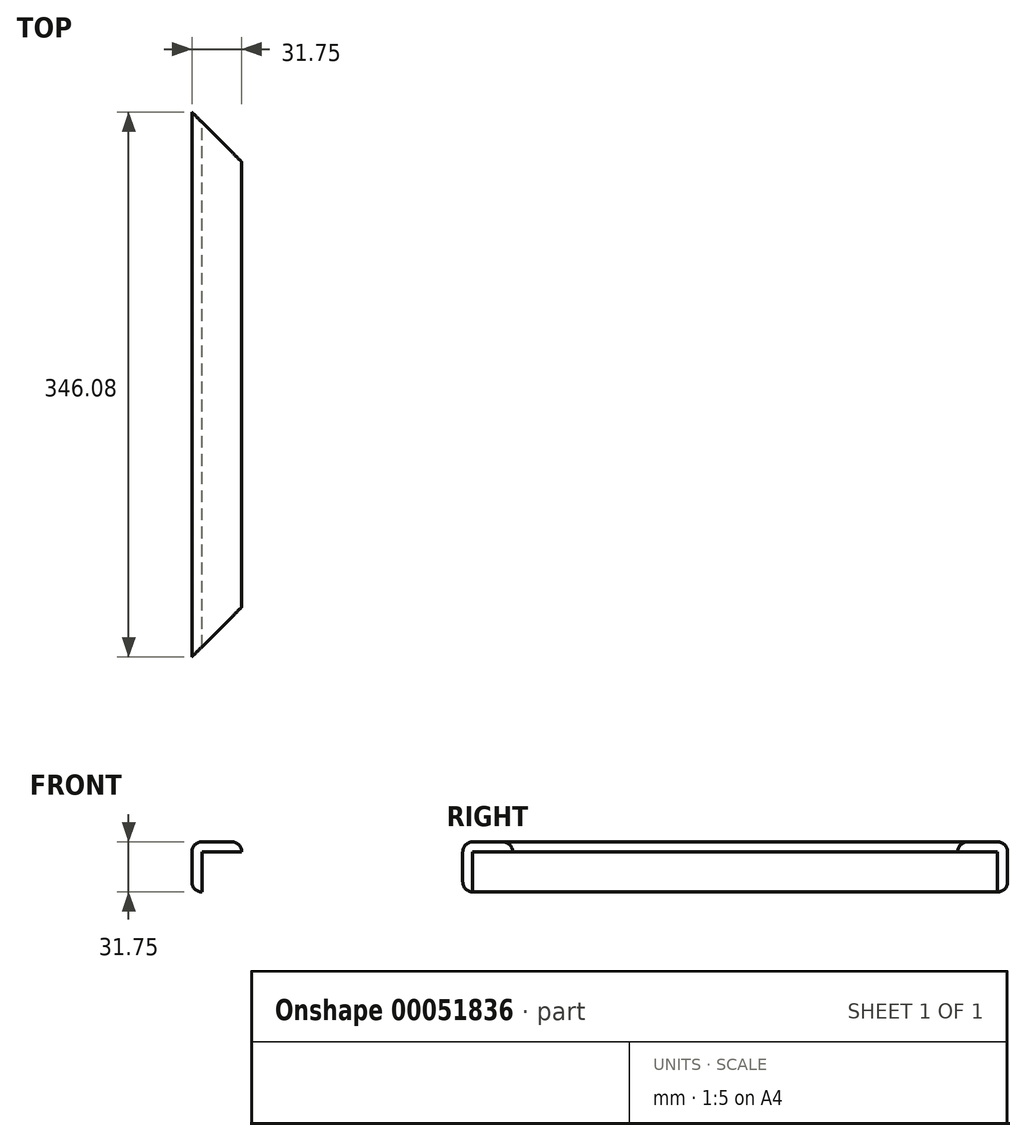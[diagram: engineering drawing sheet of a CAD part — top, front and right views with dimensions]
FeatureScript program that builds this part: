
annotation { "Feature Type Name" : "Feature", "Feature Type Description" : "" }
export const myFeature = defineFeature(function(context is Context, id is Id, definition is map)
    precondition{}
    {
        {
            var Q0;
            Q0=qCreatedBy(makeId("Front.planeOp"),FACE);
            var sketch = newSketch(context, id + "F0", { "sketchPlane" : qUnion([Q0])});
            skLineSegment(sketch, "E0", {"start": v(0, 0) * mm, "end": v(0, -25.4) * mm});
            skLineSegment(sketch, "E1", {"start": v(0, 0) * mm, "end": v(25.4, 0) * mm});
            skLineSegment(sketch, "E2.0", {"start": v(-6.35, 0) * mm, "end": v(-6.35, -19.05) * mm});
            skLineSegment(sketch, "E3.0", {"start": v(0, 6.35) * mm, "end": v(19.05, 6.35) * mm});
            skLineSegment(sketch, "E4", {"start": v(25.4, 0) * mm, "end": v(25.4, 0) * mm});
            skLineSegment(sketch, "E5", {"start": v(0, -25.4) * mm, "end": v(0, -25.4) * mm});
            skPoint(sketch, "E6.visualSharp", {"position": v(-6.35, -25.4) * mm});
            skArc(sketch, "E6.filletArc", {"start": v(-6.35, -19.05) * mm, "mid": v(-4.5, -23.54) * mm, "end": v(0, -25.4) * mm});
            skPoint(sketch, "E7.visualSharp", {"position": v(-6.35, 6.35) * mm});
            skArc(sketch, "E7.filletArc", {"start": v(0, 6.35) * mm, "mid": v(-4.5, 4.5) * mm, "end": v(-6.35, 0) * mm});
            skPoint(sketch, "E8.visualSharp", {"position": v(25.4, 6.35) * mm});
            skArc(sketch, "E8.filletArc", {"start": v(25.4, 0) * mm, "mid": v(23.54, 4.5) * mm, "end": v(19.05, 6.35) * mm});
            skSolve(sketch);
        }
        {
            var Q0;
            Q0=makeQuery(id+"F0.imprint","IMPRINT",FACE,{"disambiguationData":[TD([[makeQuery(id+"F0.imprint","IMPRINT",EDGE,{"derivedFrom":sQuery(id+"F0.wireOp",EDGE,"E0")}),-1.0]])]});
            extrude(context, id + "F1", {"entities" : qUnion([Q0]), "depth" : 346.07 * mm});
        }
        {
            var Q0;
            Q0=makeQuery(id+"F1.opExtrude","SWEPT_FACE",FACE,{"disambiguationData":[OSD([sQuery(id+"F0.wireOp",EDGE,"E3.0")])]});
            var sketch = newSketch(context, id + "F2", { "sketchPlane" : qUnion([Q0])});
            skLineSegment(sketch, "E9", {"start": v(-6.35, -346.08) * mm, "end": v(31.07, -308.66) * mm});
            skLineSegment(sketch, "E10", {"start": v(25.95, -346.08) * mm, "end": v(-6.35, -346.08) * mm});
            skPoint(sketch, "E10.startSnap0", {"position": v(9.52, -346.08) * mm});
            skLineSegment(sketch, "E11", {"start": v(31.07, -308.66) * mm, "end": v(25.95, -346.08) * mm});
            skSolve(sketch);
        }
        {
            var Q0;
            {var subQ0=sQuery(id+"F2.wireOp",EDGE,"E11");Q0=makeQuery(id+"F2.imprint","IMPRINT",FACE,{"disambiguationData":[TD([[makeQuery(id+"F2.imprint","IMPRINT",EDGE,{"derivedFrom":subQ0}),-1.0]])]});}
            var Q1;
            {var subQ0=sQuery(id+"F2.wireOp",EDGE,"E9");var subQ1=sQuery(id+"F0.wireOp",EDGE,"E3.0");var subQ2=makeQuery(id+"F1.opExtrude","SWEPT_EDGE",EDGE,{"disambiguationData":[OSD([subQ1,sQuery(id+"F0.wireOp",EDGE,"E7.filletArc")])]});var subQ3=makeQuery(id+"F2.imprint","INTERSECT",VERTEX,{"derivedFrom":[subQ2,subQ0]});Q1=makeQuery(id+"F2.imprint","IMPRINT",FACE,{"disambiguationData":[TD([[makeQuery(id+"F2.imprint","IMPRINT",EDGE,{"disambiguationData":[TD([[subQ3,-1.0]])],"derivedFrom":subQ0}),-1.0]])]});}
            var Q2;
            {var subQ0=sQuery(id+"F2.wireOp",EDGE,"E10");var subQ1=sQuery(id+"F2.wireOp",EDGE,"E9");var subQ2=makeQuery(id+"F2.imprint","INTERSECT",VERTEX,{"derivedFrom":[subQ1,subQ0]});Q2=makeQuery(id+"F2.imprint","IMPRINT",FACE,{"disambiguationData":[TD([[makeQuery(id+"F2.imprint","IMPRINT",EDGE,{"disambiguationData":[TD([[subQ2,-1.0]])],"derivedFrom":subQ1}),-1.0]])]});}
            extrude(context, id + "F3", {"entities" : qUnion([Q0, Q1, Q2]), "operationType" : NewBodyOperationType.REMOVE, "endBound" : BoundingType.UP_TO_NEXT, "oppositeDirection" : true, "depth" : 25.4 * mm});
        }
        {
            var Q0;
            Q0=makeQuery(id+"F1.opExtrude","SWEPT_FACE",FACE,{"disambiguationData":[OSD([sQuery(id+"F0.wireOp",EDGE,"E3.0")])]});
            var sketch = newSketch(context, id + "F4", { "sketchPlane" : qUnion([Q0])});
            skLineSegment(sketch, "E12", {"start": v(-6.35, 0) * mm, "end": v(25.4, -31.75) * mm});
            skLineSegment(sketch, "E13", {"start": v(25.4, -31.75) * mm, "end": v(25.4, 0) * mm});
            skLineSegment(sketch, "E14", {"start": v(25.4, 0) * mm, "end": v(-6.35, 0) * mm});
            skSolve(sketch);
        }
        {
            var Q0;
            Q0 = qSketchRegion(id + "F4", true);
            extrude(context, id + "F5", {"entities" : qUnion([Q0]), "operationType" : NewBodyOperationType.REMOVE, "oppositeDirection" : true, "depth" : 38.1 * mm});
        }
    });
